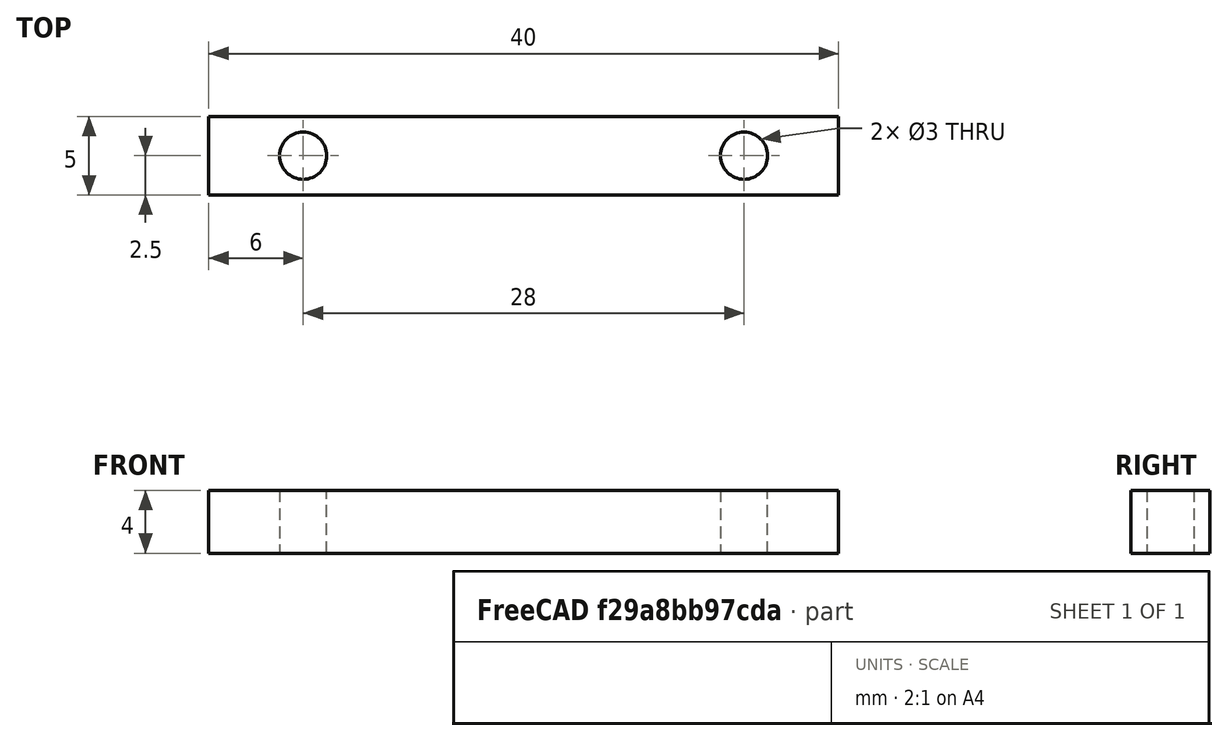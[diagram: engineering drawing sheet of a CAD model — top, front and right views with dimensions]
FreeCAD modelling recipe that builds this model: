
FCSTD DOCUMENT  (FreeCAD 0.20R)
Label: soporte tornillos arduino 1
License: All rights reserved
LicenseURL: http://en.wikipedia.org/wiki/All_rights_reserved
objects: Sketcher::SketchObject×1, PartDesign::Pad×1, PartDesign::Body×1
note: 4 computed .brp shape members not serialized (recipe doc carries the construction recipe); baked Part::Feature solids carry a one-line shape summary decoded from their .brp

FEATURE [Sketcher::SketchObject] Sketch
  FullyConstrained = true
  MapMode = 5
  Support = -> [XY_Plane]
  sketch-geometry (10):
    g0: Circle CenterX=-14 CenterY=0 CenterZ=0 NormalX=0 NormalY=0 NormalZ=1 AngleXU=0 Radius=1.5
    g1: Circle CenterX=14 CenterY=0 CenterZ=0 NormalX=0 NormalY=0 NormalZ=1 AngleXU=0 Radius=1.5
    g2: LineSegment StartX=-14 StartY=0 StartZ=0 EndX=0 EndY=0 EndZ=0
    g3: LineSegment StartX=0 StartY=0 StartZ=0 EndX=14 EndY=0 EndZ=0
    g4: LineSegment StartX=-20 StartY=2.5 StartZ=0 EndX=20 EndY=2.5 EndZ=0
    g5: LineSegment StartX=20 StartY=2.5 StartZ=0 EndX=20 EndY=-2.5 EndZ=0
    g6: LineSegment StartX=20 StartY=-2.5 StartZ=0 EndX=-20 EndY=-2.5 EndZ=0
    g7: LineSegment StartX=-20 StartY=-2.5 StartZ=0 EndX=-20 EndY=2.5 EndZ=0
    g8: LineSegment StartX=-20 StartY=2.5 StartZ=0 EndX=0 EndY=0 EndZ=0
    g9: LineSegment StartX=0 StartY=0 StartZ=0 EndX=20 EndY=-2.5 EndZ=0
  constraints (26):
    c: PointOnObject(g0,g-1)
    c: PointOnObject(g1,g-1)
    c: Equal(g0,g1)
    c: Coincident(g2,g0)
    c: Coincident(g2,g-1)
    c: Coincident(g3,g-1)
    c: Coincident(g3,g1)
    c: Equal(g3,g2)
    c: DistanceX(g0,g1) = 28
    c: Diameter(g1) = 3
    c: Coincident(g4,g5)
    c: Coincident(g5,g6)
    c: Coincident(g6,g7)
    c: Coincident(g7,g4)
    c: Horizontal(g4)
    c: Horizontal(g6)
    c: Vertical(g5)
    c: Vertical(g7)
    c: Coincident(g8,g4)
    c: Coincident(g8,g-1)
    c: Coincident(g9,g-1)
    c: Coincident(g9,g5)
    c: Equal(g9,g8)
    c: Parallel(g8,g9)
    c: DistanceX(g6,g5) = 40
    c: DistanceY(g7,g7) = 5
FEATURE [PartDesign::Pad] Pad
  Direction = (0,0,1)
  Length = 4
  Length2 = 100
  Profile = -> Sketch
  ReferenceAxis = -> Sketch [N_Axis]
  Type = 0
FEATURE [PartDesign::Body] Body
  Group = -> [Sketch,Pad]
  Origin = -> Origin
  Tip = -> Pad
